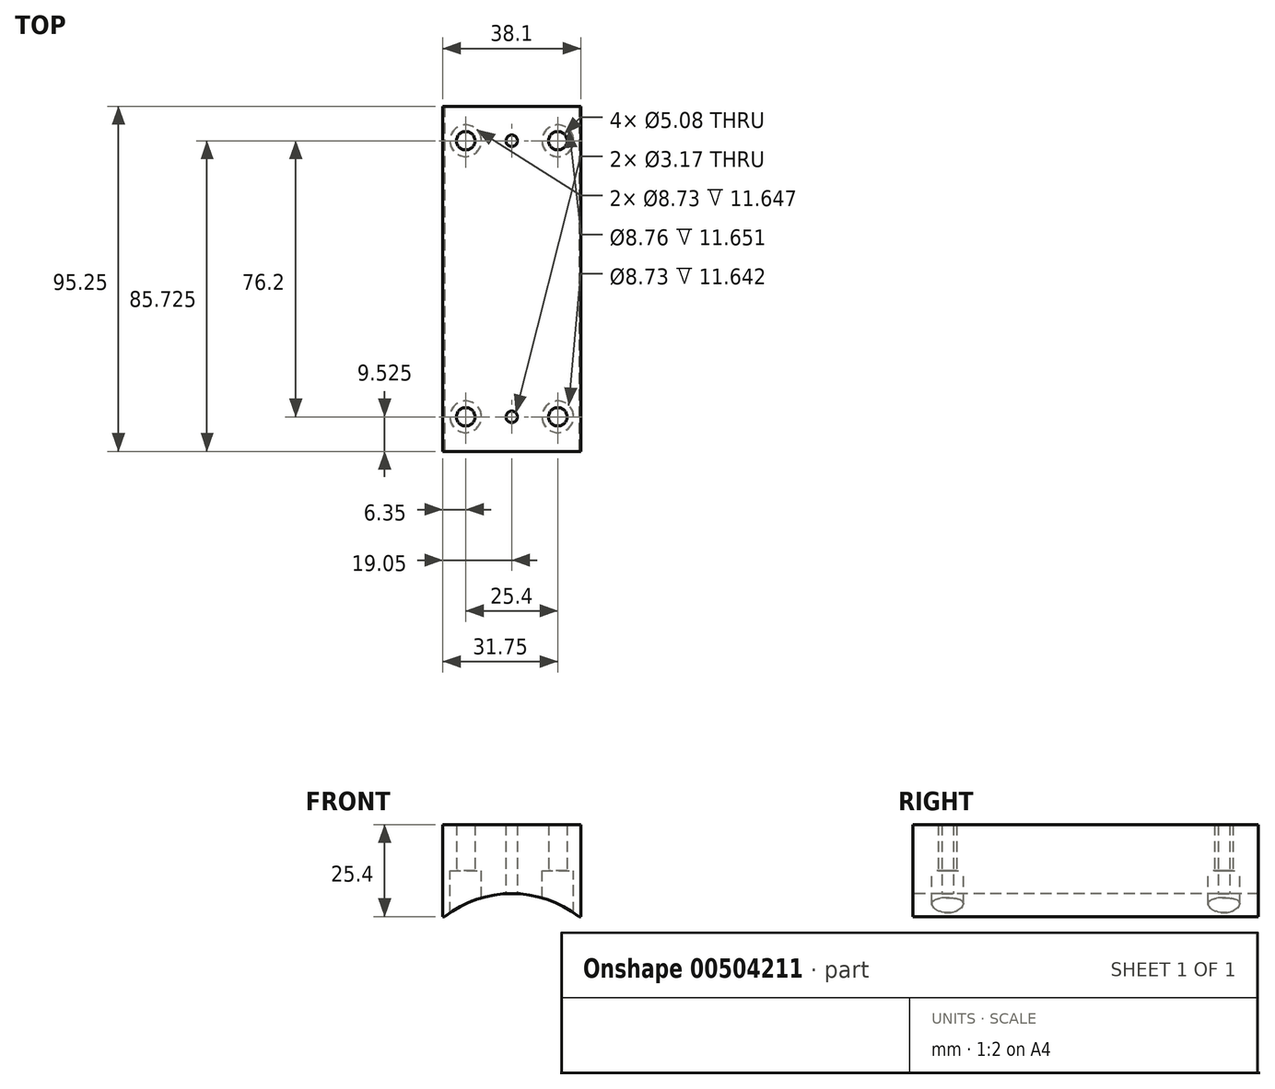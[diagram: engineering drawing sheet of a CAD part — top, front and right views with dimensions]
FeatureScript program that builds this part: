
annotation { "Feature Type Name" : "Feature", "Feature Type Description" : "" }
export const myFeature = defineFeature(function(context is Context, id is Id, definition is map)
    precondition{}
    {
        {
            var Q0;
            Q0=qCreatedBy(makeId("Top.planeOp"),FACE);
            var sketch = newSketch(context, id + "F0", { "sketchPlane" : qUnion([Q0])});
            skLineSegment(sketch, "E0.bottom", {"start": v(-19.05, -47.63) * mm, "end": v(19.05, -47.63) * mm});
            skLineSegment(sketch, "E0.top", {"start": v(-19.05, 47.63) * mm, "end": v(19.05, 47.63) * mm});
            skLineSegment(sketch, "E0.left", {"start": v(-19.05, -47.63) * mm, "end": v(-19.05, 47.63) * mm});
            skLineSegment(sketch, "E0.right", {"start": v(19.05, -47.63) * mm, "end": v(19.05, 47.63) * mm});
            skPoint(sketch, "E0.middle", {"position": v(0, 0) * mm});
            skCircle(sketch, "E1", {"center": v(0, 38.1) * mm, "radius": 1.59 * mm});
            skCircle(sketch, "E2", {"center": v(0, -38.1) * mm, "radius": 1.59 * mm});
            skCircle(sketch, "E3", {"center": v(-12.7, -38.1) * mm, "radius": 2.54 * mm});
            skCircle(sketch, "E4", {"center": v(12.7, -38.1) * mm, "radius": 2.54 * mm});
            skCircle(sketch, "E5", {"center": v(-12.7, 38.1) * mm, "radius": 2.54 * mm});
            skCircle(sketch, "E6", {"center": v(12.7, 38.1) * mm, "radius": 2.54 * mm});
            skSolve(sketch);
        }
        {
            var Q0;
            Q0=makeQuery(id+"F0.imprint","IMPRINT",FACE,{"disambiguationData":[TD([[makeQuery(id+"F0.imprint","IMPRINT",EDGE,{"derivedFrom":sQuery(id+"F0.wireOp",EDGE,"E0.bottom")}),1.0]])]});
            extrude(context, id + "F1", {"entities" : qUnion([Q0]), "depth" : 12.7 * mm, "offsetDistance" : 25.4 * mm});
        }
        {
            var Q0;
            Q0=makeQuery(id+"F1.opExtrude","SWEPT_BODY",BODY,{"disambiguationData":[OSD([sQuery(id+"F0.wireOp",EDGE,"E0.bottom"),sQuery(id+"F0.wireOp",EDGE,"E0.top"),sQuery(id+"F0.wireOp",EDGE,"E0.left"),sQuery(id+"F0.wireOp",EDGE,"E0.right"),sQuery(id+"F0.wireOp",EDGE,"E1"),sQuery(id+"F0.wireOp",EDGE,"E2"),sQuery(id+"F0.wireOp",EDGE,"E3"),sQuery(id+"F0.wireOp",EDGE,"E4"),sQuery(id+"F0.wireOp",EDGE,"E5"),sQuery(id+"F0.wireOp",EDGE,"E6")])]});
            var Q1;
            Q1=qCreatedBy(makeId("Front.planeOp"),FACE);
            transform(context, id + "F2", {"entities" : qUnion([Q0]), "transformType" : TransformType.TRANSLATION_DISTANCE, "transformDirection" : qUnion([Q1]), "distance" : 47.62 * mm, "oppositeDirection" : true, "makeCopy" : false});
        }
        {
            var Q0;
            Q0=makeQuery(id+"F1.opExtrude","CAP_FACE",FACE,{"disambiguationData":[OSD([sQuery(id+"F0.wireOp",EDGE,"E0.bottom"),sQuery(id+"F0.wireOp",EDGE,"E0.top"),sQuery(id+"F0.wireOp",EDGE,"E0.left"),sQuery(id+"F0.wireOp",EDGE,"E0.right"),sQuery(id+"F0.wireOp",EDGE,"E1"),sQuery(id+"F0.wireOp",EDGE,"E2"),sQuery(id+"F0.wireOp",EDGE,"E3"),sQuery(id+"F0.wireOp",EDGE,"E4"),sQuery(id+"F0.wireOp",EDGE,"E5"),sQuery(id+"F0.wireOp",EDGE,"E6")])],"isStart":true});
            var sketch = newSketch(context, id + "F3", { "sketchPlane" : qUnion([Q0])});
            skLineSegment(sketch, "E7.bottom", {"start": v(-19.05, 0) * mm, "end": v(19.05, 0) * mm});
            skLineSegment(sketch, "E7.top", {"start": v(-19.05, -95.25) * mm, "end": v(19.05, -95.25) * mm});
            skLineSegment(sketch, "E7.left", {"start": v(-19.05, 0) * mm, "end": v(-19.05, -95.25) * mm});
            skLineSegment(sketch, "E7.right", {"start": v(19.05, 0) * mm, "end": v(19.05, -95.25) * mm});
            skCircle(sketch, "E8", {"center": v(0, -9.52) * mm, "radius": 1.59 * mm});
            skCircle(sketch, "E9", {"center": v(-12.7, -9.52) * mm, "radius": 4.37 * mm});
            skCircle(sketch, "E10", {"center": v(12.7, -9.52) * mm, "radius": 4.37 * mm});
            skCircle(sketch, "E11", {"center": v(-12.7, -85.73) * mm, "radius": 4.37 * mm});
            skCircle(sketch, "E12", {"center": v(0, -85.72) * mm, "radius": 1.59 * mm});
            skCircle(sketch, "E13", {"center": v(12.7, -85.73) * mm, "radius": 4.38 * mm});
            skSolve(sketch);
        }
        {
            var Q0;
            Q0=makeQuery(id+"F3.imprint","IMPRINT",FACE,{"disambiguationData":[TD([[makeQuery(id+"F3.imprint","IMPRINT",EDGE,{"derivedFrom":sQuery(id+"F3.wireOp",EDGE,"E7.bottom")}),-1.0]])]});
            extrude(context, id + "F4", {"entities" : qUnion([Q0]), "operationType" : NewBodyOperationType.ADD, "depth" : 12.7 * mm, "offsetDistance" : 25.4 * mm});
        }
        {
            var Q0;
            Q0=qCreatedBy(makeId("Front.planeOp"),FACE);
            var sketch = newSketch(context, id + "F5", { "sketchPlane" : qUnion([Q0])});
            skCircle(sketch, "E14", {"center": v(0, -36.51) * mm, "radius": 30.16 * mm});
            skSolve(sketch);
        }
        {
            var Q0;
            Q0=makeQuery(id+"F5.imprint","IMPRINT",FACE,{"disambiguationData":[TD([[makeQuery(id+"F5.imprint","IMPRINT",EDGE,{"derivedFrom":sQuery(id+"F5.wireOp",EDGE,"E14")}),1.0]])]});
            extrude(context, id + "F6", {"entities" : qUnion([Q0]), "operationType" : NewBodyOperationType.REMOVE, "oppositeDirection" : true, "depth" : 95.25 * mm, "offsetDistance" : 25.4 * mm});
        }
    });
